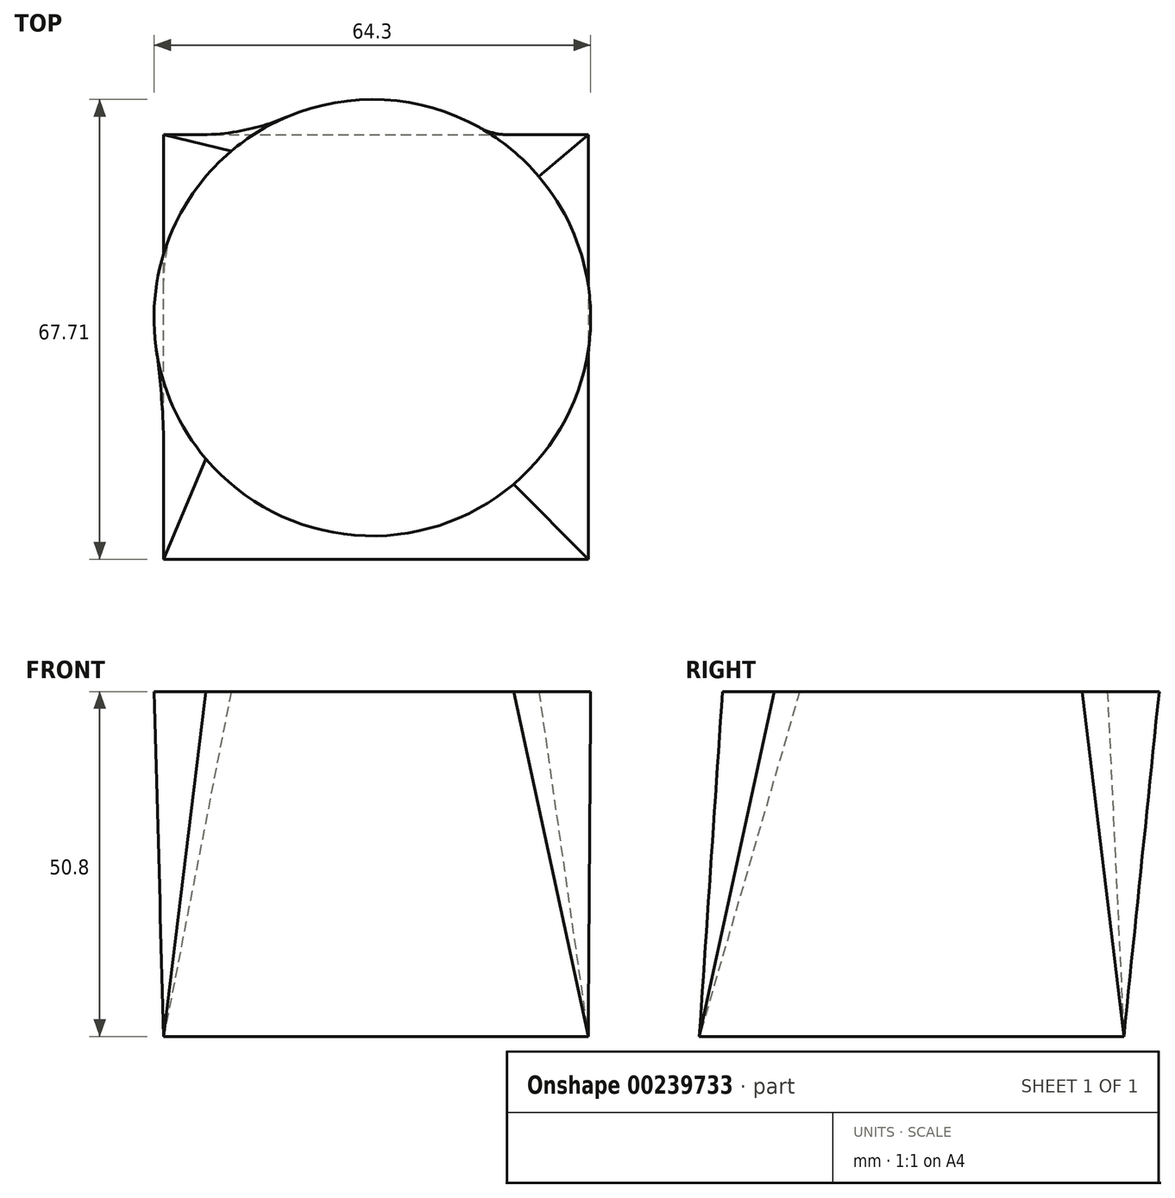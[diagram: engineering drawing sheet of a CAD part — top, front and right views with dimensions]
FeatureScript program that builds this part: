
annotation { "Feature Type Name" : "Feature", "Feature Type Description" : "" }
export const myFeature = defineFeature(function(context is Context, id is Id, definition is map)
    precondition{}
    {
        {
            var Q0;
            Q0=qCreatedBy(makeId("Top.planeOp"),FACE);
            var sketch = newSketch(context, id + "F0", { "sketchPlane" : qUnion([Q0])});
            skCircle(sketch, "E0.cCircle", {"center": v(7.8, -33.82) * mm, "radius": 31.25 * mm, "construction": true});
            skLineSegment(sketch, "E0.0", {"start": v(39.04, -2.57) * mm, "end": v(39.04, -65.07) * mm});
            skLineSegment(sketch, "E0.1", {"start": v(39.04, -65.07) * mm, "end": v(-23.45, -65.07) * mm});
            skLineSegment(sketch, "E0.2", {"start": v(-23.45, -65.07) * mm, "end": v(-23.45, -2.57) * mm});
            skLineSegment(sketch, "E0.3", {"start": v(-23.45, -2.57) * mm, "end": v(39.04, -2.57) * mm});
            skPoint(sketch, "E0.0.midPoint", {"position": v(39.04, -33.82) * mm});
            skSolve(sketch);
        }
        {
            var Q0;
            Q0=qCreatedBy(makeId("Top.planeOp"),FACE);
            cPlane(context, id + "F1", {"entities" : qUnion([Q0]), "cplaneType" : CPlaneType.OFFSET, "offset" : 50.8 * mm, "width" : 152.4 * mm, "height" : 152.4 * mm});
        }
        {
            var Q0;
            Q0=qCreatedBy(id+"F1.planeOp",FACE);
            var sketch = newSketch(context, id + "F2", { "sketchPlane" : qUnion([Q0])});
            skCircle(sketch, "E1", {"center": v(7.27, -29.51) * mm, "radius": 32.15 * mm});
            skSolve(sketch);
        }
        {
            var Q0;
            Q0=makeQuery(id+"F2.imprint","IMPRINT",FACE,{"disambiguationData":[TD([[makeQuery(id+"F2.imprint","IMPRINT",EDGE,{"derivedFrom":sQuery(id+"F2.wireOp",EDGE,"E1")}),1.0]])]});
            var Q1;
            Q1=makeQuery(id+"F0.imprint","IMPRINT",FACE,{"disambiguationData":[TD([[makeQuery(id+"F0.imprint","IMPRINT",EDGE,{"derivedFrom":sQuery(id+"F0.wireOp",EDGE,"E0.0")}),-1.0]])]});
            loft(context, id + "F3", {"sheetProfilesArray" : [{ "sheetProfileEntities" : qUnion([Q0]) }, { "sheetProfileEntities" : qUnion([Q1]) }]});
        }
    });
